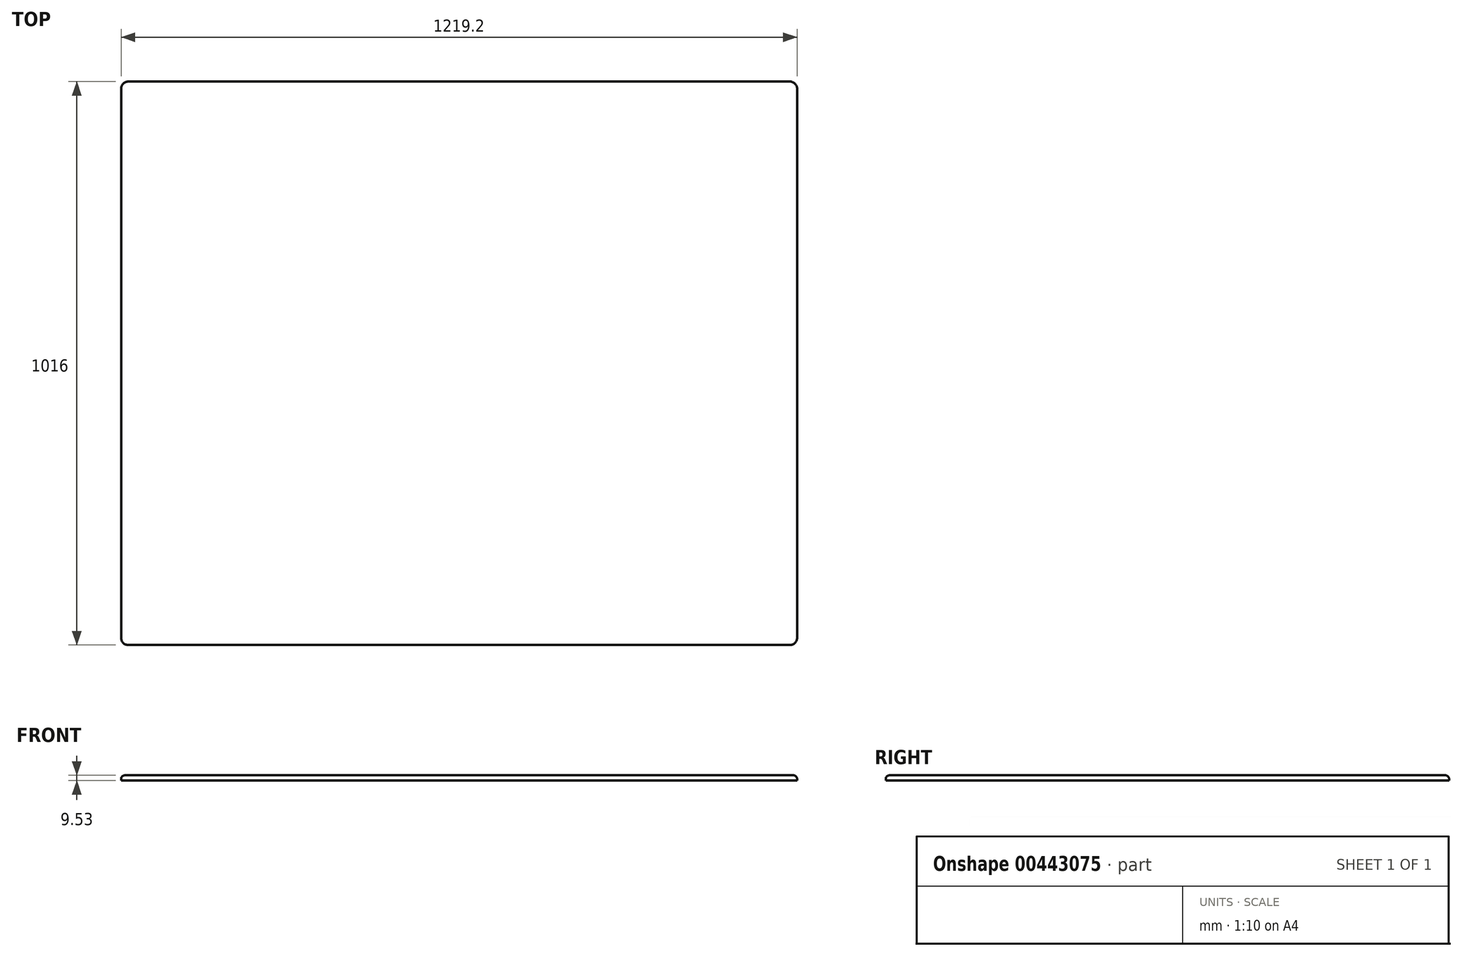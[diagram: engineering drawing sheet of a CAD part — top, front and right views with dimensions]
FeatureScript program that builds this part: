
annotation { "Feature Type Name" : "Feature", "Feature Type Description" : "" }
export const myFeature = defineFeature(function(context is Context, id is Id, definition is map)
    precondition{}
    {
        {
            var Q0;
            Q0=qCreatedBy(makeId("Front.planeOp"),FACE);
            var sketch = newSketch(context, id + "F0", { "sketchPlane" : qUnion([Q0])});
            skLineSegment(sketch, "E0.bottom", {"start": v(0, 0) * mm, "end": v(1219.2, 0) * mm});
            skLineSegment(sketch, "E0.top", {"start": v(0, 9.53) * mm, "end": v(1219.2, 9.53) * mm});
            skLineSegment(sketch, "E0.left", {"start": v(0, 0) * mm, "end": v(0, 9.53) * mm});
            skLineSegment(sketch, "E0.right", {"start": v(1219.2, 0) * mm, "end": v(1219.2, 9.53) * mm});
            skSolve(sketch);
        }
        {
            var Q0;
            Q0 = qSketchRegion(id + "F0", true);
            extrude(context, id + "F1", {"entities" : qUnion([Q0]), "endBound" : BoundingType.SYMMETRIC, "depth" : 1016 * mm});
        }
        {
            var Q0;
            Q0=makeQuery(id+"F1.opExtrude","CAP_EDGE",EDGE,{"disambiguationData":[OSD([sQuery(id+"F0.wireOp",EDGE,"E0.right")])],"isStart":false});
            var Q1;
            Q1=makeQuery(id+"F1.opExtrude","CAP_EDGE",EDGE,{"disambiguationData":[OSD([sQuery(id+"F0.wireOp",EDGE,"E0.right")])],"isStart":true});
            var Q2;
            Q2=makeQuery(id+"F1.opExtrude","CAP_EDGE",EDGE,{"disambiguationData":[OSD([sQuery(id+"F0.wireOp",EDGE,"E0.left")])],"isStart":true});
            var Q3;
            Q3=makeQuery(id+"F1.opExtrude","CAP_EDGE",EDGE,{"disambiguationData":[OSD([sQuery(id+"F0.wireOp",EDGE,"E0.left")])],"isStart":false});
            fillet(context, id + "F2", {"entities" : qUnion([Q0, Q1, Q2, Q3]), "radius" : 12.7 * mm, "tangentPropagation" : true, "allowEdgeOverflow" : false});
        }
        {
            var Q0;
            Q0=makeQuery(id+"F1.opExtrude","SWEPT_FACE",FACE,{"disambiguationData":[OSD([sQuery(id+"F0.wireOp",EDGE,"E0.top")])]});
            fillet(context, id + "F3", {"entities" : qUnion([Q0]), "radius" : 6.35 * mm, "tangentPropagation" : true, "allowEdgeOverflow" : false});
        }
    });
